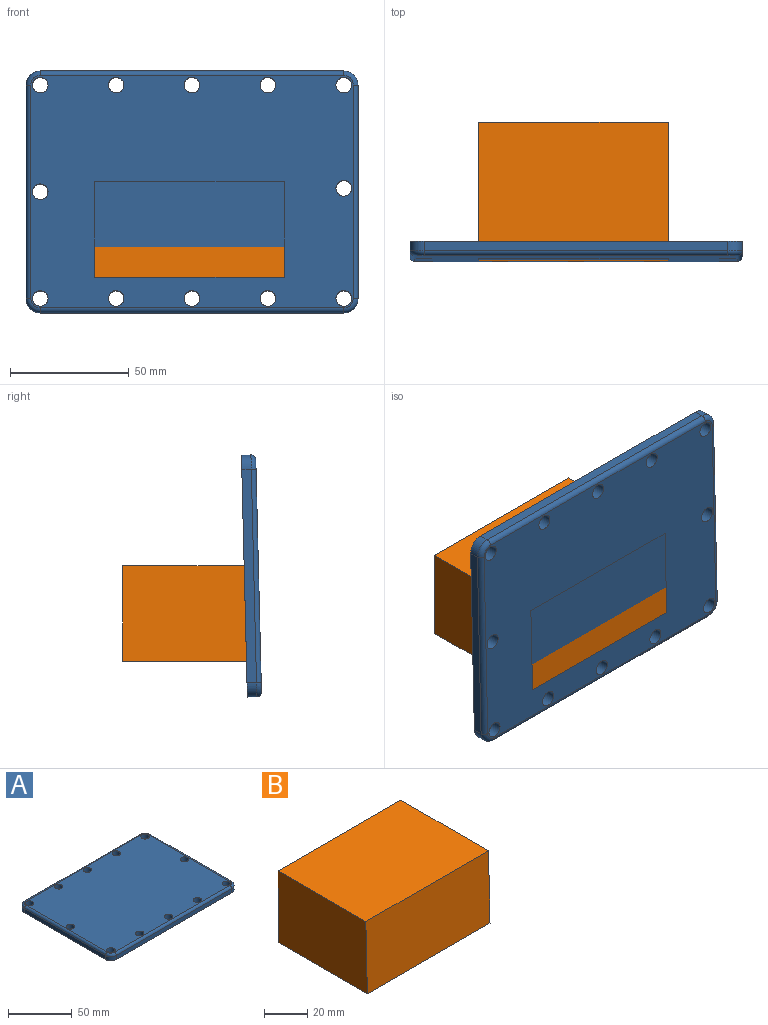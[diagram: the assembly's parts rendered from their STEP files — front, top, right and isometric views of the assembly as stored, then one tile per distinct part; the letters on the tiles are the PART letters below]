
ASSEMBLY  parts=2 mates=1
PART A: 30 faces, bbox 141x103x6 mm
  f0: plane 90x4mm, normal (-1,0,0), area 360mm2, adj f1,f19,f21,f25
  f1: cylinder r=6mm len=6mm, axis (0,0,-1), area 37.7mm2, adj f0,f2,f21,f27
  f2: plane 128x4mm, normal (0,-1,0), area 512mm2, adj f1,f3,f21,f29
  f3: cylinder r=6mm len=6mm, axis (0,0,-1), area 37.7mm2, adj f2,f4,f21,f28
  f4: plane 90x4mm, normal (1,0,0), area 360mm2, adj f3,f5,f21,f26
  f5: cylinder r=6mm len=6mm, axis (0,0,-1), area 37.7mm2, adj f4,f6,f21,f24
  f6: plane 128x4mm, normal (0,1,0), area 512mm2, adj f5,f19,f21,f22
  f7: cylinder r=3.3mm len=6.6mm, axis (0,0,-1), area 124.4mm2, adj f20,f21
  f8: cylinder r=3.3mm len=6.6mm, axis (0,0,-1), area 124.4mm2, adj f20,f21
  f9: cylinder r=3.3mm len=6.6mm, axis (0,0,-1), area 124.4mm2, adj f20,f21
  f10: cylinder r=3.3mm len=6.6mm, axis (0,0,-1), area 124.4mm2, adj f20,f21
  f11: cylinder r=3.3mm len=6.6mm, axis (0,0,-1), area 124.4mm2, adj f20,f21
  f12: cylinder r=3.3mm len=6.6mm, axis (0,0,-1), area 124.4mm2, adj f20,f21
  f13: cylinder r=3.3mm len=6.6mm, axis (0,0,-1), area 124.4mm2, adj f20,f21
  f14: cylinder r=3.3mm len=6.6mm, axis (0,0,-1), area 124.4mm2, adj f20,f21
  f15: cylinder r=3.3mm len=6.6mm, axis (0,0,-1), area 124.4mm2, adj f20,f21
  f16: cylinder r=3.3mm len=6.6mm, axis (0,0,-1), area 124.4mm2, adj f20,f21
  f17: cylinder r=3.3mm len=6.6mm, axis (0,0,-1), area 124.4mm2, adj f20,f21
  f18: cylinder r=3.3mm len=6.6mm, axis (0,0,-1), area 124.4mm2, adj f20,f21
  f19: cylinder r=6mm len=6mm, axis (0,0,-1), area 37.7mm2, adj f0,f6,f21,f23
  f20: plane 136x98mm, normal (0,0,1), area 12903.7mm2, adj f7,f8,f9,f10,f11,f12,f13,f14
  f21: plane 140x102mm, normal (0,0,-1), area 13838.6mm2, adj f0,f1,f2,f3,f4,f5,f6,f7
  f22: cylinder r=2mm len=128mm, axis (1,0,0), area 402.1mm2, adj f6,f20,f23,f24
  f23: torus R=4mm, axis (0,0,1), area 26mm2, adj f19,f20,f22,f25
  f24: torus R=4mm, axis (0,0,1), area 26mm2, adj f5,f20,f22,f26
  f25: cylinder r=2mm len=90mm, axis (0,1,0), area 282.7mm2, adj f0,f20,f23,f27
  f26: cylinder r=2mm len=90mm, axis (0,-1,0), area 282.7mm2, adj f4,f20,f24,f28
  f27: torus R=4mm, axis (0,0,1), area 26mm2, adj f1,f20,f25,f29
  f28: torus R=4mm, axis (0,0,1), area 26mm2, adj f3,f20,f26,f29
  f29: cylinder r=2mm len=128mm, axis (-1,0,0), area 402.1mm2, adj f2,f20,f27,f28
PART B: 6 faces, bbox 80x58.3x40.4 mm
  f0: plane 80x40.36mm, normal (0,-1,0.02), area 3229.7mm2, adj f1,f3,f4,f5
  f1: plane 80x58.27mm, normal (0,0,-1), area 4661.5mm2, adj f0,f2,f4,f5
  f2: plane 80x40.36mm, normal (0,1,0), area 3228.7mm2, adj f1,f3,f4,f5
  f3: plane 80x57.28mm, normal (0,0,1), area 4582.6mm2, adj f0,f2,f4,f5
  f4: plane 58.27x40.36mm, normal (1,0,0), area 2331.7mm2, adj f0,f1,f2,f3
  f5: plane 58.27x40.36mm, normal (-1,0,0), area 2331.7mm2, adj f0,f1,f2,f3
PLACE A rot(axis=(1,0,0),88.6deg) t=(-25.25,-43.09,19.31)mm
PLACE B t=(-25.77,-19.35,-28.36)mm
MATE planar A.f20 <-> B.f0  axis (0,-1,0.02) through (-24.68,-49.16,16.32)mm
